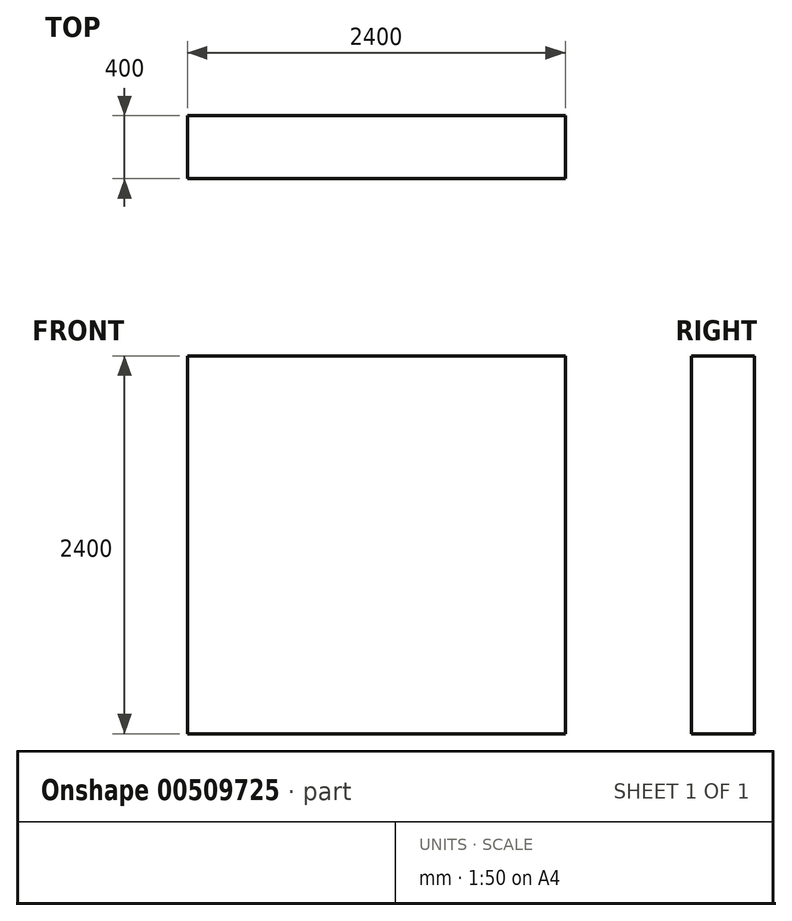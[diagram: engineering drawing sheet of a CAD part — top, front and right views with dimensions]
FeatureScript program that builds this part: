
annotation { "Feature Type Name" : "Feature", "Feature Type Description" : "" }
export const myFeature = defineFeature(function(context is Context, id is Id, definition is map)
    precondition{}
    {
        {
            var Q0;
            Q0=qCreatedBy(makeId("Front.planeOp"),FACE);
            var sketch = newSketch(context, id + "F0", { "sketchPlane" : qUnion([Q0])});
            skLineSegment(sketch, "E0.bottom", {"start": v(0, 0) * mm, "end": v(2400, 0) * mm});
            skLineSegment(sketch, "E0.top", {"start": v(0, 2400) * mm, "end": v(2400, 2400) * mm});
            skLineSegment(sketch, "E0.left", {"start": v(0, 0) * mm, "end": v(0, 2400) * mm});
            skLineSegment(sketch, "E0.right", {"start": v(2400, 0) * mm, "end": v(2400, 2400) * mm});
            skSolve(sketch);
        }
        {
            var Q0;
            Q0 = qSketchRegion(id + "F0", true);
            extrude(context, id + "F1", {"entities" : qUnion([Q0]), "depth" : 400 * mm});
        }
    });
